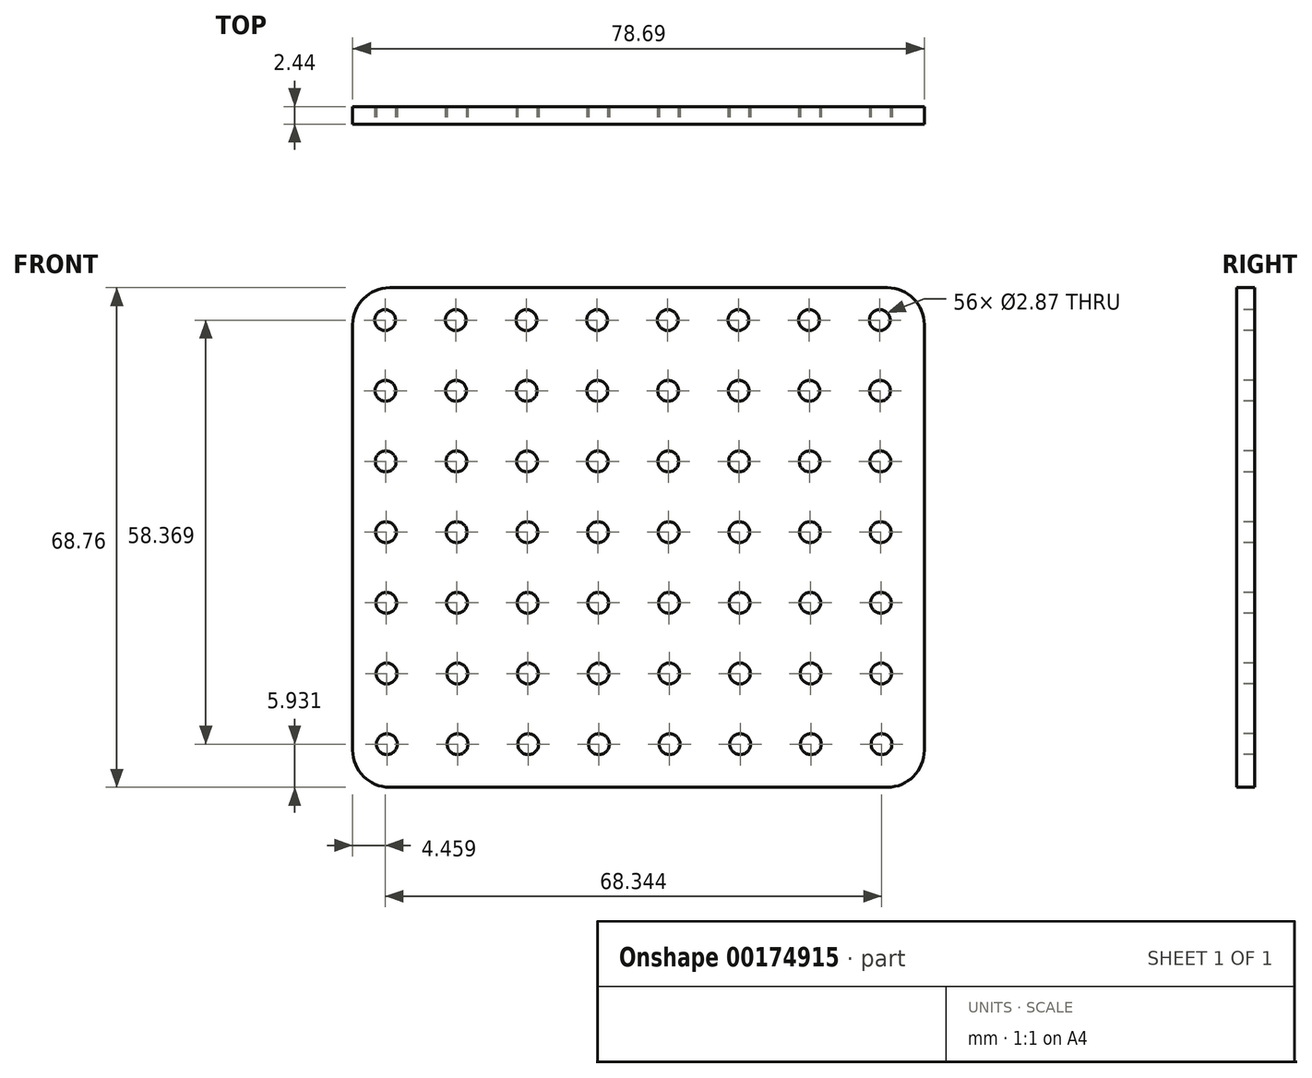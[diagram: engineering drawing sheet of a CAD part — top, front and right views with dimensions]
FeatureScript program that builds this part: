
annotation { "Feature Type Name" : "Feature", "Feature Type Description" : "" }
export const myFeature = defineFeature(function(context is Context, id is Id, definition is map)
    precondition{}
    {
        {
            var Q0;
            Q0=qCreatedBy(makeId("Front.planeOp"),FACE);
            var sketch = newSketch(context, id + "F0", { "sketchPlane" : qUnion([Q0])});
            skLineSegment(sketch, "E0.bottom", {"start": v(0, 0) * mm, "end": v(-78.69, 0) * mm});
            skLineSegment(sketch, "E0.top", {"start": v(0, 68.76) * mm, "end": v(-78.69, 68.76) * mm});
            skLineSegment(sketch, "E0.left", {"start": v(0, 0) * mm, "end": v(0, 68.76) * mm});
            skLineSegment(sketch, "E0.right", {"start": v(-78.69, 0) * mm, "end": v(-78.69, 68.76) * mm});
            skSolve(sketch);
        }
        {
            var Q0;
            Q0=makeQuery(id+"F0.imprint","IMPRINT",FACE,{"disambiguationData":[TD([[makeQuery(id+"F0.imprint","IMPRINT",EDGE,{"derivedFrom":sQuery(id+"F0.wireOp",EDGE,"E0.bottom")}),-1.0]])]});
            extrude(context, id + "F1", {"entities" : qUnion([Q0]), "depth" : 2.44 * mm});
        }
        {
            var Q0;
            Q0=makeQuery(id+"F1.opExtrude","CAP_FACE",FACE,{"disambiguationData":[OSD([sQuery(id+"F0.wireOp",EDGE,"E0.bottom"),sQuery(id+"F0.wireOp",EDGE,"E0.top"),sQuery(id+"F0.wireOp",EDGE,"E0.left"),sQuery(id+"F0.wireOp",EDGE,"E0.right")])],"isStart":false});
            var sketch = newSketch(context, id + "F2", { "sketchPlane" : qUnion([Q0])});
            skCircle(sketch, "E1", {"center": v(-74.23, 64.3) * mm, "radius": 1.44 * mm});
            skCircle(sketch, "E2.1.0.0", {"center": v(-64.5, 64.3) * mm, "radius": 1.44 * mm});
            skCircle(sketch, "E2.2.0.0", {"center": v(-54.78, 64.3) * mm, "radius": 1.44 * mm});
            skCircle(sketch, "E2.3.0.0", {"center": v(-45.05, 64.3) * mm, "radius": 1.44 * mm});
            skCircle(sketch, "E2.4.0.0", {"center": v(-35.32, 64.3) * mm, "radius": 1.44 * mm});
            skCircle(sketch, "E2.5.0.0", {"center": v(-25.6, 64.3) * mm, "radius": 1.44 * mm});
            skCircle(sketch, "E2.6.0.0", {"center": v(-15.86, 64.3) * mm, "radius": 1.44 * mm});
            skCircle(sketch, "E2.7.0.0", {"center": v(-6.13, 64.3) * mm, "radius": 1.44 * mm});
            skLineSegment(sketch, "E2.direction1", {"start": v(-74.23, 64.3) * mm, "end": v(-64.5, 64.3) * mm, "construction": true});
            skCircle(sketch, "E3.1.0.0", {"center": v(-74.2, 54.57) * mm, "radius": 1.44 * mm});
            skCircle(sketch, "E3.1.0.1", {"center": v(-64.46, 54.57) * mm, "radius": 1.44 * mm});
            skCircle(sketch, "E3.1.0.2", {"center": v(-54.73, 54.57) * mm, "radius": 1.44 * mm});
            skCircle(sketch, "E3.1.0.3", {"center": v(-45, 54.57) * mm, "radius": 1.44 * mm});
            skCircle(sketch, "E3.1.0.4", {"center": v(-35.28, 54.57) * mm, "radius": 1.44 * mm});
            skCircle(sketch, "E3.1.0.5", {"center": v(-25.55, 54.57) * mm, "radius": 1.44 * mm});
            skCircle(sketch, "E3.1.0.6", {"center": v(-15.82, 54.57) * mm, "radius": 1.44 * mm});
            skCircle(sketch, "E3.1.0.7", {"center": v(-6.1, 54.57) * mm, "radius": 1.44 * mm});
            skCircle(sketch, "E3.2.0.0", {"center": v(-74.15, 44.84) * mm, "radius": 1.44 * mm});
            skCircle(sketch, "E3.2.0.1", {"center": v(-64.42, 44.84) * mm, "radius": 1.44 * mm});
            skCircle(sketch, "E3.2.0.2", {"center": v(-54.7, 44.84) * mm, "radius": 1.44 * mm});
            skCircle(sketch, "E3.2.0.3", {"center": v(-44.96, 44.84) * mm, "radius": 1.44 * mm});
            skCircle(sketch, "E3.2.0.4", {"center": v(-35.24, 44.84) * mm, "radius": 1.44 * mm});
            skCircle(sketch, "E3.2.0.5", {"center": v(-25.5, 44.84) * mm, "radius": 1.44 * mm});
            skCircle(sketch, "E3.2.0.6", {"center": v(-15.78, 44.84) * mm, "radius": 1.44 * mm});
            skCircle(sketch, "E3.2.0.7", {"center": v(-6.05, 44.84) * mm, "radius": 1.44 * mm});
            skCircle(sketch, "E3.3.0.0", {"center": v(-74.1, 35.12) * mm, "radius": 1.44 * mm});
            skCircle(sketch, "E3.3.0.1", {"center": v(-64.38, 35.12) * mm, "radius": 1.44 * mm});
            skCircle(sketch, "E3.3.0.2", {"center": v(-54.65, 35.12) * mm, "radius": 1.44 * mm});
            skCircle(sketch, "E3.3.0.3", {"center": v(-44.92, 35.12) * mm, "radius": 1.44 * mm});
            skCircle(sketch, "E3.3.0.4", {"center": v(-35.2, 35.12) * mm, "radius": 1.44 * mm});
            skCircle(sketch, "E3.3.0.5", {"center": v(-25.47, 35.12) * mm, "radius": 1.44 * mm});
            skCircle(sketch, "E3.3.0.6", {"center": v(-15.74, 35.12) * mm, "radius": 1.44 * mm});
            skCircle(sketch, "E3.3.0.7", {"center": v(-6.01, 35.12) * mm, "radius": 1.44 * mm});
            skCircle(sketch, "E3.4.0.0", {"center": v(-74.07, 25.39) * mm, "radius": 1.44 * mm});
            skCircle(sketch, "E3.4.0.1", {"center": v(-64.34, 25.39) * mm, "radius": 1.44 * mm});
            skCircle(sketch, "E3.4.0.2", {"center": v(-54.61, 25.39) * mm, "radius": 1.44 * mm});
            skCircle(sketch, "E3.4.0.3", {"center": v(-44.88, 25.39) * mm, "radius": 1.44 * mm});
            skCircle(sketch, "E3.4.0.4", {"center": v(-35.15, 25.39) * mm, "radius": 1.44 * mm});
            skCircle(sketch, "E3.4.0.5", {"center": v(-25.43, 25.39) * mm, "radius": 1.44 * mm});
            skCircle(sketch, "E3.4.0.6", {"center": v(-15.7, 25.39) * mm, "radius": 1.44 * mm});
            skCircle(sketch, "E3.4.0.7", {"center": v(-5.97, 25.39) * mm, "radius": 1.44 * mm});
            skCircle(sketch, "E3.5.0.0", {"center": v(-74.03, 15.66) * mm, "radius": 1.44 * mm});
            skCircle(sketch, "E3.5.0.1", {"center": v(-64.3, 15.66) * mm, "radius": 1.44 * mm});
            skCircle(sketch, "E3.5.0.2", {"center": v(-54.57, 15.66) * mm, "radius": 1.44 * mm});
            skCircle(sketch, "E3.5.0.3", {"center": v(-44.84, 15.66) * mm, "radius": 1.44 * mm});
            skCircle(sketch, "E3.5.0.4", {"center": v(-35.11, 15.66) * mm, "radius": 1.44 * mm});
            skCircle(sketch, "E3.5.0.5", {"center": v(-25.38, 15.66) * mm, "radius": 1.44 * mm});
            skCircle(sketch, "E3.5.0.6", {"center": v(-15.66, 15.66) * mm, "radius": 1.44 * mm});
            skCircle(sketch, "E3.5.0.7", {"center": v(-5.93, 15.66) * mm, "radius": 1.44 * mm});
            skCircle(sketch, "E3.6.0.0", {"center": v(-73.98, 5.93) * mm, "radius": 1.44 * mm});
            skCircle(sketch, "E3.6.0.1", {"center": v(-64.26, 5.93) * mm, "radius": 1.44 * mm});
            skCircle(sketch, "E3.6.0.2", {"center": v(-54.53, 5.93) * mm, "radius": 1.44 * mm});
            skCircle(sketch, "E3.6.0.3", {"center": v(-44.8, 5.93) * mm, "radius": 1.44 * mm});
            skCircle(sketch, "E3.6.0.4", {"center": v(-35.07, 5.93) * mm, "radius": 1.44 * mm});
            skCircle(sketch, "E3.6.0.5", {"center": v(-25.34, 5.93) * mm, "radius": 1.44 * mm});
            skCircle(sketch, "E3.6.0.6", {"center": v(-15.62, 5.93) * mm, "radius": 1.44 * mm});
            skCircle(sketch, "E3.6.0.7", {"center": v(-5.89, 5.93) * mm, "radius": 1.44 * mm});
            skLineSegment(sketch, "E3.direction1", {"start": v(-74.23, 64.3) * mm, "end": v(-74.2, 54.57) * mm, "construction": true});
            skSolve(sketch);
        }
        {
            var Q0;
            Q0=makeQuery(id+"F2.imprint","IMPRINT",FACE,{"disambiguationData":[TD([[makeQuery(id+"F2.imprint","IMPRINT",EDGE,{"derivedFrom":sQuery(id+"F2.wireOp",EDGE,"E1")}),1.0]])]});
            var Q1;
            Q1=makeQuery(id+"F2.imprint","IMPRINT",FACE,{"disambiguationData":[TD([[makeQuery(id+"F2.imprint","IMPRINT",EDGE,{"derivedFrom":sQuery(id+"F2.wireOp",EDGE,"E2.1.0.0")}),1.0]])]});
            var Q2;
            Q2=makeQuery(id+"F2.imprint","IMPRINT",FACE,{"disambiguationData":[TD([[makeQuery(id+"F2.imprint","IMPRINT",EDGE,{"derivedFrom":sQuery(id+"F2.wireOp",EDGE,"E2.2.0.0")}),1.0]])]});
            var Q3;
            Q3=makeQuery(id+"F2.imprint","IMPRINT",FACE,{"disambiguationData":[TD([[makeQuery(id+"F2.imprint","IMPRINT",EDGE,{"derivedFrom":sQuery(id+"F2.wireOp",EDGE,"E2.3.0.0")}),1.0]])]});
            var Q4;
            Q4=makeQuery(id+"F2.imprint","IMPRINT",FACE,{"disambiguationData":[TD([[makeQuery(id+"F2.imprint","IMPRINT",EDGE,{"derivedFrom":sQuery(id+"F2.wireOp",EDGE,"E2.4.0.0")}),1.0]])]});
            var Q5;
            Q5=makeQuery(id+"F2.imprint","IMPRINT",FACE,{"disambiguationData":[TD([[makeQuery(id+"F2.imprint","IMPRINT",EDGE,{"derivedFrom":sQuery(id+"F2.wireOp",EDGE,"E2.6.0.0")}),1.0]])]});
            var Q6;
            Q6=makeQuery(id+"F2.imprint","IMPRINT",FACE,{"disambiguationData":[TD([[makeQuery(id+"F2.imprint","IMPRINT",EDGE,{"derivedFrom":sQuery(id+"F2.wireOp",EDGE,"E2.7.0.0")}),1.0]])]});
            var Q7;
            Q7=makeQuery(id+"F2.imprint","IMPRINT",FACE,{"disambiguationData":[TD([[makeQuery(id+"F2.imprint","IMPRINT",EDGE,{"derivedFrom":sQuery(id+"F2.wireOp",EDGE,"E3.1.0.0")}),1.0]])]});
            var Q8;
            Q8=makeQuery(id+"F2.imprint","IMPRINT",FACE,{"disambiguationData":[TD([[makeQuery(id+"F2.imprint","IMPRINT",EDGE,{"derivedFrom":sQuery(id+"F2.wireOp",EDGE,"E3.1.0.1")}),1.0]])]});
            var Q9;
            Q9=makeQuery(id+"F2.imprint","IMPRINT",FACE,{"disambiguationData":[TD([[makeQuery(id+"F2.imprint","IMPRINT",EDGE,{"derivedFrom":sQuery(id+"F2.wireOp",EDGE,"E3.1.0.2")}),1.0]])]});
            var Q10;
            Q10=makeQuery(id+"F2.imprint","IMPRINT",FACE,{"disambiguationData":[TD([[makeQuery(id+"F2.imprint","IMPRINT",EDGE,{"derivedFrom":sQuery(id+"F2.wireOp",EDGE,"E3.1.0.3")}),1.0]])]});
            var Q11;
            Q11=makeQuery(id+"F2.imprint","IMPRINT",FACE,{"disambiguationData":[TD([[makeQuery(id+"F2.imprint","IMPRINT",EDGE,{"derivedFrom":sQuery(id+"F2.wireOp",EDGE,"E3.1.0.4")}),1.0]])]});
            var Q12;
            Q12=makeQuery(id+"F2.imprint","IMPRINT",FACE,{"disambiguationData":[TD([[makeQuery(id+"F2.imprint","IMPRINT",EDGE,{"derivedFrom":sQuery(id+"F2.wireOp",EDGE,"E3.1.0.7")}),1.0]])]});
            var Q13;
            Q13=makeQuery(id+"F2.imprint","IMPRINT",FACE,{"disambiguationData":[TD([[makeQuery(id+"F2.imprint","IMPRINT",EDGE,{"derivedFrom":sQuery(id+"F2.wireOp",EDGE,"E2.5.0.0")}),1.0]])]});
            var Q14;
            Q14=makeQuery(id+"F2.imprint","IMPRINT",FACE,{"disambiguationData":[TD([[makeQuery(id+"F2.imprint","IMPRINT",EDGE,{"derivedFrom":sQuery(id+"F2.wireOp",EDGE,"E3.1.0.5")}),1.0]])]});
            var Q15;
            Q15=makeQuery(id+"F2.imprint","IMPRINT",FACE,{"disambiguationData":[TD([[makeQuery(id+"F2.imprint","IMPRINT",EDGE,{"derivedFrom":sQuery(id+"F2.wireOp",EDGE,"E3.2.0.0")}),1.0]])]});
            var Q16;
            Q16=makeQuery(id+"F2.imprint","IMPRINT",FACE,{"disambiguationData":[TD([[makeQuery(id+"F2.imprint","IMPRINT",EDGE,{"derivedFrom":sQuery(id+"F2.wireOp",EDGE,"E3.2.0.2")}),1.0]])]});
            var Q17;
            Q17=makeQuery(id+"F2.imprint","IMPRINT",FACE,{"disambiguationData":[TD([[makeQuery(id+"F2.imprint","IMPRINT",EDGE,{"derivedFrom":sQuery(id+"F2.wireOp",EDGE,"E3.2.0.3")}),1.0]])]});
            var Q18;
            Q18=makeQuery(id+"F2.imprint","IMPRINT",FACE,{"disambiguationData":[TD([[makeQuery(id+"F2.imprint","IMPRINT",EDGE,{"derivedFrom":sQuery(id+"F2.wireOp",EDGE,"E3.2.0.5")}),1.0]])]});
            var Q19;
            Q19=makeQuery(id+"F2.imprint","IMPRINT",FACE,{"disambiguationData":[TD([[makeQuery(id+"F2.imprint","IMPRINT",EDGE,{"derivedFrom":sQuery(id+"F2.wireOp",EDGE,"E3.2.0.7")}),1.0]])]});
            var Q20;
            Q20=makeQuery(id+"F2.imprint","IMPRINT",FACE,{"disambiguationData":[TD([[makeQuery(id+"F2.imprint","IMPRINT",EDGE,{"derivedFrom":sQuery(id+"F2.wireOp",EDGE,"E3.3.0.2")}),1.0]])]});
            var Q21;
            Q21=makeQuery(id+"F2.imprint","IMPRINT",FACE,{"disambiguationData":[TD([[makeQuery(id+"F2.imprint","IMPRINT",EDGE,{"derivedFrom":sQuery(id+"F2.wireOp",EDGE,"E3.3.0.3")}),1.0]])]});
            var Q22;
            Q22=makeQuery(id+"F2.imprint","IMPRINT",FACE,{"disambiguationData":[TD([[makeQuery(id+"F2.imprint","IMPRINT",EDGE,{"derivedFrom":sQuery(id+"F2.wireOp",EDGE,"E3.3.0.4")}),1.0]])]});
            var Q23;
            Q23=makeQuery(id+"F2.imprint","IMPRINT",FACE,{"disambiguationData":[TD([[makeQuery(id+"F2.imprint","IMPRINT",EDGE,{"derivedFrom":sQuery(id+"F2.wireOp",EDGE,"E3.3.0.6")}),1.0]])]});
            var Q24;
            Q24=makeQuery(id+"F2.imprint","IMPRINT",FACE,{"disambiguationData":[TD([[makeQuery(id+"F2.imprint","IMPRINT",EDGE,{"derivedFrom":sQuery(id+"F2.wireOp",EDGE,"E3.3.0.7")}),1.0]])]});
            var Q25;
            Q25=makeQuery(id+"F2.imprint","IMPRINT",FACE,{"disambiguationData":[TD([[makeQuery(id+"F2.imprint","IMPRINT",EDGE,{"derivedFrom":sQuery(id+"F2.wireOp",EDGE,"E3.4.0.0")}),1.0]])]});
            var Q26;
            Q26=makeQuery(id+"F2.imprint","IMPRINT",FACE,{"disambiguationData":[TD([[makeQuery(id+"F2.imprint","IMPRINT",EDGE,{"derivedFrom":sQuery(id+"F2.wireOp",EDGE,"E3.4.0.1")}),1.0]])]});
            var Q27;
            Q27=makeQuery(id+"F2.imprint","IMPRINT",FACE,{"disambiguationData":[TD([[makeQuery(id+"F2.imprint","IMPRINT",EDGE,{"derivedFrom":sQuery(id+"F2.wireOp",EDGE,"E3.4.0.3")}),1.0]])]});
            var Q28;
            Q28=makeQuery(id+"F2.imprint","IMPRINT",FACE,{"disambiguationData":[TD([[makeQuery(id+"F2.imprint","IMPRINT",EDGE,{"derivedFrom":sQuery(id+"F2.wireOp",EDGE,"E3.4.0.4")}),1.0]])]});
            var Q29;
            Q29=makeQuery(id+"F2.imprint","IMPRINT",FACE,{"disambiguationData":[TD([[makeQuery(id+"F2.imprint","IMPRINT",EDGE,{"derivedFrom":sQuery(id+"F2.wireOp",EDGE,"E3.4.0.5")}),1.0]])]});
            var Q30;
            Q30=makeQuery(id+"F2.imprint","IMPRINT",FACE,{"disambiguationData":[TD([[makeQuery(id+"F2.imprint","IMPRINT",EDGE,{"derivedFrom":sQuery(id+"F2.wireOp",EDGE,"E3.4.0.7")}),1.0]])]});
            var Q31;
            Q31=makeQuery(id+"F2.imprint","IMPRINT",FACE,{"disambiguationData":[TD([[makeQuery(id+"F2.imprint","IMPRINT",EDGE,{"derivedFrom":sQuery(id+"F2.wireOp",EDGE,"E3.5.0.0")}),1.0]])]});
            var Q32;
            Q32=makeQuery(id+"F2.imprint","IMPRINT",FACE,{"disambiguationData":[TD([[makeQuery(id+"F2.imprint","IMPRINT",EDGE,{"derivedFrom":sQuery(id+"F2.wireOp",EDGE,"E3.5.0.1")}),1.0]])]});
            var Q33;
            Q33=makeQuery(id+"F2.imprint","IMPRINT",FACE,{"disambiguationData":[TD([[makeQuery(id+"F2.imprint","IMPRINT",EDGE,{"derivedFrom":sQuery(id+"F2.wireOp",EDGE,"E3.5.0.3")}),1.0]])]});
            var Q34;
            Q34=makeQuery(id+"F2.imprint","IMPRINT",FACE,{"disambiguationData":[TD([[makeQuery(id+"F2.imprint","IMPRINT",EDGE,{"derivedFrom":sQuery(id+"F2.wireOp",EDGE,"E3.5.0.5")}),1.0]])]});
            var Q35;
            Q35=makeQuery(id+"F2.imprint","IMPRINT",FACE,{"disambiguationData":[TD([[makeQuery(id+"F2.imprint","IMPRINT",EDGE,{"derivedFrom":sQuery(id+"F2.wireOp",EDGE,"E3.2.0.1")}),1.0]])]});
            var Q36;
            Q36=makeQuery(id+"F2.imprint","IMPRINT",FACE,{"disambiguationData":[TD([[makeQuery(id+"F2.imprint","IMPRINT",EDGE,{"derivedFrom":sQuery(id+"F2.wireOp",EDGE,"E3.2.0.4")}),1.0]])]});
            var Q37;
            Q37=makeQuery(id+"F2.imprint","IMPRINT",FACE,{"disambiguationData":[TD([[makeQuery(id+"F2.imprint","IMPRINT",EDGE,{"derivedFrom":sQuery(id+"F2.wireOp",EDGE,"E3.2.0.6")}),1.0]])]});
            var Q38;
            Q38=makeQuery(id+"F2.imprint","IMPRINT",FACE,{"disambiguationData":[TD([[makeQuery(id+"F2.imprint","IMPRINT",EDGE,{"derivedFrom":sQuery(id+"F2.wireOp",EDGE,"E3.3.0.0")}),1.0]])]});
            var Q39;
            Q39=makeQuery(id+"F2.imprint","IMPRINT",FACE,{"disambiguationData":[TD([[makeQuery(id+"F2.imprint","IMPRINT",EDGE,{"derivedFrom":sQuery(id+"F2.wireOp",EDGE,"E3.3.0.1")}),1.0]])]});
            var Q40;
            Q40=makeQuery(id+"F2.imprint","IMPRINT",FACE,{"disambiguationData":[TD([[makeQuery(id+"F2.imprint","IMPRINT",EDGE,{"derivedFrom":sQuery(id+"F2.wireOp",EDGE,"E3.3.0.5")}),1.0]])]});
            var Q41;
            Q41=makeQuery(id+"F2.imprint","IMPRINT",FACE,{"disambiguationData":[TD([[makeQuery(id+"F2.imprint","IMPRINT",EDGE,{"derivedFrom":sQuery(id+"F2.wireOp",EDGE,"E3.4.0.6")}),1.0]])]});
            var Q42;
            Q42=makeQuery(id+"F2.imprint","IMPRINT",FACE,{"disambiguationData":[TD([[makeQuery(id+"F2.imprint","IMPRINT",EDGE,{"derivedFrom":sQuery(id+"F2.wireOp",EDGE,"E3.5.0.2")}),1.0]])]});
            var Q43;
            Q43=makeQuery(id+"F2.imprint","IMPRINT",FACE,{"disambiguationData":[TD([[makeQuery(id+"F2.imprint","IMPRINT",EDGE,{"derivedFrom":sQuery(id+"F2.wireOp",EDGE,"E3.5.0.6")}),1.0]])]});
            var Q44;
            Q44=makeQuery(id+"F2.imprint","IMPRINT",FACE,{"disambiguationData":[TD([[makeQuery(id+"F2.imprint","IMPRINT",EDGE,{"derivedFrom":sQuery(id+"F2.wireOp",EDGE,"E3.6.0.2")}),1.0]])]});
            var Q45;
            Q45=makeQuery(id+"F2.imprint","IMPRINT",FACE,{"disambiguationData":[TD([[makeQuery(id+"F2.imprint","IMPRINT",EDGE,{"derivedFrom":sQuery(id+"F2.wireOp",EDGE,"E3.6.0.3")}),1.0]])]});
            var Q46;
            Q46=makeQuery(id+"F2.imprint","IMPRINT",FACE,{"disambiguationData":[TD([[makeQuery(id+"F2.imprint","IMPRINT",EDGE,{"derivedFrom":sQuery(id+"F2.wireOp",EDGE,"E3.6.0.5")}),1.0]])]});
            var Q47;
            Q47=makeQuery(id+"F2.imprint","IMPRINT",FACE,{"disambiguationData":[TD([[makeQuery(id+"F2.imprint","IMPRINT",EDGE,{"derivedFrom":sQuery(id+"F2.wireOp",EDGE,"E3.6.0.6")}),1.0]])]});
            var Q48;
            Q48=makeQuery(id+"F2.imprint","IMPRINT",FACE,{"disambiguationData":[TD([[makeQuery(id+"F2.imprint","IMPRINT",EDGE,{"derivedFrom":sQuery(id+"F2.wireOp",EDGE,"E3.1.0.6")}),1.0]])]});
            var Q49;
            Q49=makeQuery(id+"F2.imprint","IMPRINT",FACE,{"disambiguationData":[TD([[makeQuery(id+"F2.imprint","IMPRINT",EDGE,{"derivedFrom":sQuery(id+"F2.wireOp",EDGE,"E3.4.0.2")}),1.0]])]});
            var Q50;
            Q50=makeQuery(id+"F2.imprint","IMPRINT",FACE,{"disambiguationData":[TD([[makeQuery(id+"F2.imprint","IMPRINT",EDGE,{"derivedFrom":sQuery(id+"F2.wireOp",EDGE,"E3.5.0.7")}),1.0]])]});
            var Q51;
            Q51=makeQuery(id+"F2.imprint","IMPRINT",FACE,{"disambiguationData":[TD([[makeQuery(id+"F2.imprint","IMPRINT",EDGE,{"derivedFrom":sQuery(id+"F2.wireOp",EDGE,"E3.6.0.4")}),1.0]])]});
            var Q52;
            Q52=makeQuery(id+"F2.imprint","IMPRINT",FACE,{"disambiguationData":[TD([[makeQuery(id+"F2.imprint","IMPRINT",EDGE,{"derivedFrom":sQuery(id+"F2.wireOp",EDGE,"E3.5.0.4")}),1.0]])]});
            var Q53;
            Q53=makeQuery(id+"F2.imprint","IMPRINT",FACE,{"disambiguationData":[TD([[makeQuery(id+"F2.imprint","IMPRINT",EDGE,{"derivedFrom":sQuery(id+"F2.wireOp",EDGE,"E3.6.0.7")}),1.0]])]});
            var Q54;
            Q54=makeQuery(id+"F2.imprint","IMPRINT",FACE,{"disambiguationData":[TD([[makeQuery(id+"F2.imprint","IMPRINT",EDGE,{"derivedFrom":sQuery(id+"F2.wireOp",EDGE,"E3.6.0.0")}),1.0]])]});
            var Q55;
            Q55=makeQuery(id+"F2.imprint","IMPRINT",FACE,{"disambiguationData":[TD([[makeQuery(id+"F2.imprint","IMPRINT",EDGE,{"derivedFrom":sQuery(id+"F2.wireOp",EDGE,"E3.6.0.1")}),1.0]])]});
            extrude(context, id + "F3", {"entities" : qUnion([Q0, Q1, Q2, Q3, Q4, Q5, Q6, Q7, Q8, Q9, Q10, Q11, Q12, Q13, Q14, Q15, Q16, Q17, Q18, Q19, Q20, Q21, Q22, Q23, Q24, Q25, Q26, Q27, Q28, Q29, Q30, Q31, Q32, Q33, Q34, Q35, Q36, Q37, Q38, Q39, Q40, Q41, Q42, Q43, Q44, Q45, Q46, Q47, Q48, Q49, Q50, Q51, Q52, Q53, Q54, Q55]), "operationType" : NewBodyOperationType.REMOVE, "oppositeDirection" : true, "depth" : 2.54 * mm});
        }
        {
            var Q0;
            Q0=makeQuery(id+"F1.opExtrude","SWEPT_EDGE",EDGE,{"disambiguationData":[OSD([sQuery(id+"F0.wireOp",EDGE,"E0.top"),sQuery(id+"F0.wireOp",EDGE,"E0.right")])]});
            var Q1;
            Q1=makeQuery(id+"F1.opExtrude","SWEPT_EDGE",EDGE,{"disambiguationData":[OSD([sQuery(id+"F0.wireOp",EDGE,"E0.bottom"),sQuery(id+"F0.wireOp",EDGE,"E0.right")])]});
            var Q2;
            Q2=makeQuery(id+"F1.opExtrude","SWEPT_EDGE",EDGE,{"disambiguationData":[OSD([sQuery(id+"F0.wireOp",EDGE,"E0.bottom"),sQuery(id+"F0.wireOp",EDGE,"E0.left")])]});
            var Q3;
            Q3=makeQuery(id+"F1.opExtrude","SWEPT_EDGE",EDGE,{"disambiguationData":[OSD([sQuery(id+"F0.wireOp",EDGE,"E0.top"),sQuery(id+"F0.wireOp",EDGE,"E0.left")])]});
            fillet(context, id + "F4", {"entities" : qUnion([Q0, Q1, Q2, Q3]), "radius" : 5.08 * mm, "tangentPropagation" : true, "allowEdgeOverflow" : false});
        }
    });
